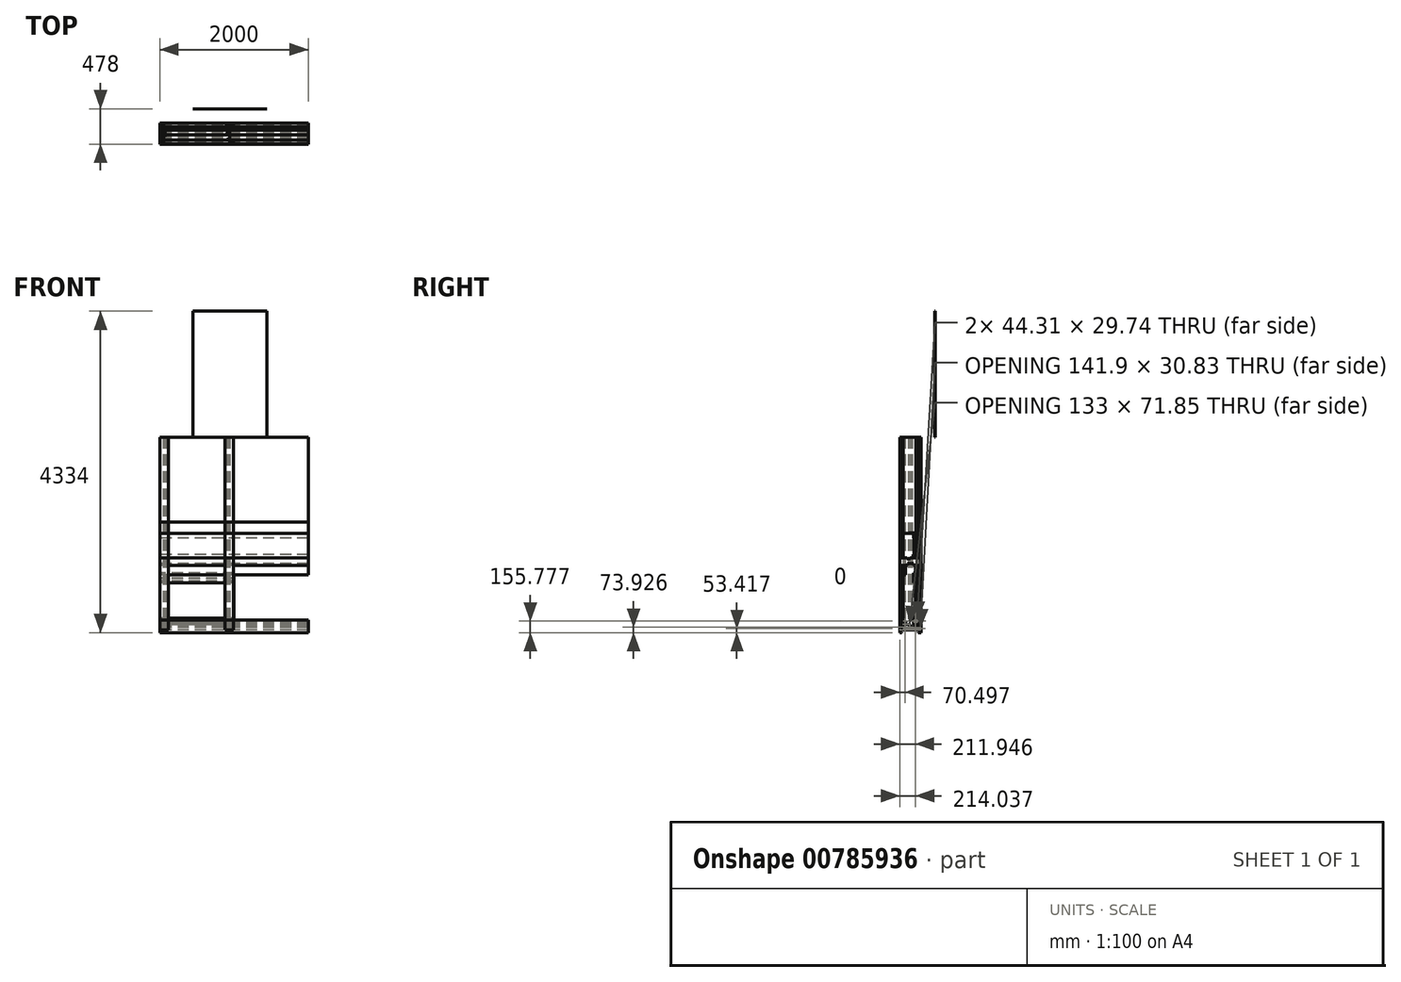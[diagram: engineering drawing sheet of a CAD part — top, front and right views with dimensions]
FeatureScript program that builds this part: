
annotation { "Feature Type Name" : "Feature", "Feature Type Description" : "" }
export const myFeature = defineFeature(function(context is Context, id is Id, definition is map)
    precondition{}
    {
        {
            var Q0;
            Q0=qCreatedBy(makeId("Top.planeOp"),FACE);
            var sketch = newSketch(context, id + "F0", { "sketchPlane" : qUnion([Q0])});
            skLineSegment(sketch, "E0", {"start": v(-131.77, 26.16) * mm, "end": v(-135.77, 26.16) * mm});
            skLineSegment(sketch, "E1", {"start": v(-135.77, 26.16) * mm, "end": v(-135.77, 70.16) * mm});
            skLineSegment(sketch, "E2", {"start": v(-135.77, 70.16) * mm, "end": v(-20.77, 70.16) * mm});
            skLineSegment(sketch, "E3", {"start": v(-20.77, 70.16) * mm, "end": v(-20.77, 66.16) * mm});
            skLineSegment(sketch, "E4", {"start": v(-20.77, 66.16) * mm, "end": v(-84.72, 66.16) * mm});
            skLineSegment(sketch, "E5", {"start": v(-84.72, 66.16) * mm, "end": v(-84.72, 4.73) * mm});
            skLineSegment(sketch, "E6", {"start": v(-84.72, 4.73) * mm, "end": v(-58.72, 4.73) * mm});
            skLineSegment(sketch, "E7", {"start": v(-58.72, 4.73) * mm, "end": v(-58.72, 6.73) * mm});
            skLineSegment(sketch, "E8", {"start": v(-58.72, 6.73) * mm, "end": v(-44.72, 0.73) * mm});
            skLineSegment(sketch, "E9", {"start": v(-44.72, 0.73) * mm, "end": v(-84.72, 0.73) * mm});
            skLineSegment(sketch, "E10", {"start": v(-84.72, 0.73) * mm, "end": v(-84.72, -93.45) * mm});
            skLineSegment(sketch, "E11", {"start": v(-84.72, -93.45) * mm, "end": v(-60.2, -93.45) * mm});
            skLineSegment(sketch, "E12", {"start": v(-60.2, -93.45) * mm, "end": v(-60.2, -73.83) * mm});
            skLineSegment(sketch, "E13", {"start": v(-60.2, -73.83) * mm, "end": v(-44.72, -73.83) * mm});
            skLineSegment(sketch, "E14", {"start": v(-44.72, -73.83) * mm, "end": v(-44.72, -79.83) * mm});
            skLineSegment(sketch, "E15", {"start": v(-44.72, -79.83) * mm, "end": v(-48.72, -79.83) * mm});
            skLineSegment(sketch, "E16", {"start": v(-48.72, -79.83) * mm, "end": v(-48.72, -77.83) * mm});
            skLineSegment(sketch, "E17", {"start": v(-48.72, -77.83) * mm, "end": v(-56.2, -77.83) * mm});
            skLineSegment(sketch, "E18", {"start": v(-56.2, -77.83) * mm, "end": v(-56.2, -93.45) * mm});
            skLineSegment(sketch, "E19", {"start": v(-56.2, -93.45) * mm, "end": v(-48.72, -93.45) * mm});
            skLineSegment(sketch, "E20", {"start": v(-48.72, -93.45) * mm, "end": v(-48.72, -91.45) * mm});
            skLineSegment(sketch, "E21", {"start": v(-48.72, -91.45) * mm, "end": v(-44.72, -91.45) * mm});
            skLineSegment(sketch, "E22", {"start": v(-44.72, -91.45) * mm, "end": v(-44.72, -97.45) * mm});
            skLineSegment(sketch, "E23", {"start": v(-44.72, -97.45) * mm, "end": v(-84.72, -97.45) * mm});
            skLineSegment(sketch, "E24", {"start": v(-84.72, -97.45) * mm, "end": v(-84.72, -212.73) * mm});
            skLineSegment(sketch, "E25", {"start": v(-84.72, -212.73) * mm, "end": v(-20.77, -212.73) * mm});
            skLineSegment(sketch, "E26", {"start": v(-20.77, -212.73) * mm, "end": v(-20.77, -216.73) * mm});
            skLineSegment(sketch, "E27", {"start": v(-20.77, -216.73) * mm, "end": v(-135.77, -216.73) * mm});
            skLineSegment(sketch, "E28", {"start": v(-135.77, -216.73) * mm, "end": v(-135.77, -172.73) * mm});
            skLineSegment(sketch, "E29", {"start": v(-135.77, -172.73) * mm, "end": v(-131.77, -172.73) * mm});
            skLineSegment(sketch, "E30", {"start": v(-131.77, -172.73) * mm, "end": v(-131.77, -212.73) * mm});
            skLineSegment(sketch, "E31", {"start": v(-131.77, -212.73) * mm, "end": v(-88.72, -212.73) * mm});
            skLineSegment(sketch, "E32", {"start": v(-88.72, -212.73) * mm, "end": v(-88.72, 66.16) * mm});
            skLineSegment(sketch, "E33", {"start": v(-88.72, 66.16) * mm, "end": v(-131.77, 66.16) * mm});
            skLineSegment(sketch, "E34", {"start": v(-131.77, 66.16) * mm, "end": v(-131.77, 26.16) * mm});
            skLineSegment(sketch, "E35.MirrorCS", {"start": v(763.76, -72.74) * mm, "end": v(763.76, -66.74) * mm});
            skLineSegment(sketch, "E36.MirrorCS", {"start": v(767.76, -66.74) * mm, "end": v(767.76, -68.74) * mm});
            skLineSegment(sketch, "E37.MirrorCS", {"start": v(767.76, -68.74) * mm, "end": v(775.23, -68.74) * mm});
            skLineSegment(sketch, "E38.MirrorCS", {"start": v(775.23, -68.74) * mm, "end": v(775.23, -53.12) * mm});
            skLineSegment(sketch, "E39.MirrorCS", {"start": v(779.23, -72.74) * mm, "end": v(763.76, -72.74) * mm});
            skLineSegment(sketch, "E40.MirrorCS", {"start": v(767.76, -53.12) * mm, "end": v(767.76, -55.12) * mm});
            skLineSegment(sketch, "E41.MirrorCS", {"start": v(763.76, -66.74) * mm, "end": v(767.76, -66.74) * mm});
            skLineSegment(sketch, "E42.MirrorCS", {"start": v(767.76, -55.12) * mm, "end": v(763.76, -55.12) * mm});
            skLineSegment(sketch, "E43.MirrorCS", {"start": v(763.76, -55.12) * mm, "end": v(763.76, -49.12) * mm});
            skLineSegment(sketch, "E44.MirrorCS", {"start": v(775.23, -53.12) * mm, "end": v(767.76, -53.12) * mm});
            skLineSegment(sketch, "E45.MirrorCS", {"start": v(779.23, -53.12) * mm, "end": v(779.23, -72.74) * mm});
            skLineSegment(sketch, "E46.MirrorCS", {"start": v(763.76, -49.12) * mm, "end": v(803.76, -49.12) * mm});
            skLineSegment(sketch, "E47.MirrorCS", {"start": v(803.76, -53.12) * mm, "end": v(779.23, -53.12) * mm});
            skLineSegment(sketch, "E48.MirrorCS", {"start": v(777.76, -153.3) * mm, "end": v(763.76, -147.3) * mm});
            skLineSegment(sketch, "E49.MirrorCS", {"start": v(850.81, -172.73) * mm, "end": v(854.81, -172.73) * mm});
            skLineSegment(sketch, "E50.MirrorCS", {"start": v(803.76, -151.3) * mm, "end": v(777.76, -151.3) * mm});
            skLineSegment(sketch, "E51.MirrorCS", {"start": v(777.76, -151.3) * mm, "end": v(777.76, -153.3) * mm});
            skLineSegment(sketch, "E52.MirrorCS", {"start": v(763.76, -147.3) * mm, "end": v(803.76, -147.3) * mm});
            skLineSegment(sketch, "E53.MirrorCS", {"start": v(739.81, -216.73) * mm, "end": v(739.81, -212.73) * mm});
            skLineSegment(sketch, "E54.MirrorCS", {"start": v(854.81, -0.01) * mm, "end": v(850.81, -0.01) * mm});
            skLineSegment(sketch, "E55.MirrorCS", {"start": v(739.81, 39.99) * mm, "end": v(739.81, 43.99) * mm});
            skLineSegment(sketch, "E56.MirrorCS", {"start": v(850.81, 39.99) * mm, "end": v(807.76, 39.99) * mm});
            skLineSegment(sketch, "E57.MirrorCS", {"start": v(803.76, -49.12) * mm, "end": v(803.76, 39.99) * mm});
            skLineSegment(sketch, "E58.MirrorCS", {"start": v(854.81, -172.73) * mm, "end": v(854.81, -216.73) * mm});
            skLineSegment(sketch, "E59.MirrorCS", {"start": v(807.76, -212.73) * mm, "end": v(850.81, -212.73) * mm});
            skLineSegment(sketch, "E60.MirrorCS", {"start": v(850.81, -0.01) * mm, "end": v(850.81, 39.99) * mm});
            skLineSegment(sketch, "E61.MirrorCS", {"start": v(854.81, -216.73) * mm, "end": v(739.81, -216.73) * mm});
            skLineSegment(sketch, "E62.MirrorCS", {"start": v(850.81, -212.73) * mm, "end": v(850.81, -172.73) * mm});
            skLineSegment(sketch, "E63.MirrorCS", {"start": v(803.76, 39.99) * mm, "end": v(739.81, 39.99) * mm});
            skLineSegment(sketch, "E64.MirrorCS", {"start": v(803.76, -147.3) * mm, "end": v(803.76, -53.12) * mm});
            skLineSegment(sketch, "E65.MirrorCS", {"start": v(803.76, -212.73) * mm, "end": v(803.76, -151.3) * mm});
            skLineSegment(sketch, "E66.MirrorCS", {"start": v(739.81, -212.73) * mm, "end": v(803.76, -212.73) * mm});
            skLineSegment(sketch, "E67.MirrorCS", {"start": v(854.81, 43.99) * mm, "end": v(854.81, -0.01) * mm});
            skLineSegment(sketch, "E68.MirrorCS", {"start": v(807.76, 39.99) * mm, "end": v(807.76, -212.73) * mm});
            skLineSegment(sketch, "E69.MirrorCS", {"start": v(739.81, 43.99) * mm, "end": v(854.81, 43.99) * mm});
            skSolve(sketch);
        }
        {
            var Q0;
            Q0=makeQuery(id+"F0.imprint","IMPRINT",FACE,{"disambiguationData":[TD([[makeQuery(id+"F0.imprint","IMPRINT",EDGE,{"derivedFrom":sQuery(id+"F0.wireOp",EDGE,"E0")}),-1.0]])]});
            extrude(context, id + "F1", {"entities" : qUnion([Q0]), "depth" : 2600 * mm, "offsetDistance" : 25 * mm});
        }
        {
            var Q0;
            Q0=makeQuery(id+"F0.imprint","IMPRINT",FACE,{"disambiguationData":[TD([[makeQuery(id+"F0.imprint","IMPRINT",EDGE,{"derivedFrom":sQuery(id+"F0.wireOp",EDGE,"E35.MirrorCS")}),-1.0]])]});
            extrude(context, id + "F2", {"entities" : qUnion([Q0]), "depth" : 2600 * mm, "offsetDistance" : 25 * mm});
        }
        {
            var Q0;
            Q0=makeQuery(id+"F1.opExtrude","SWEPT_FACE",FACE,{"disambiguationData":[OSD([sQuery(id+"F0.wireOp",EDGE,"E28")])]});
            var sketch = newSketch(context, id + "F3", { "sketchPlane" : qUnion([Q0])});
            skLineSegment(sketch, "E70", {"start": v(-70.16, -34) * mm, "end": v(-70.16, 69.03) * mm});
            skLineSegment(sketch, "E71", {"start": v(-70.16, 69.03) * mm, "end": v(-66.16, 69.03) * mm});
            skLineSegment(sketch, "E72", {"start": v(-66.16, 69.03) * mm, "end": v(-66.16, 36.25) * mm});
            skLineSegment(sketch, "E73", {"start": v(-66.16, 36.25) * mm, "end": v(-11.46, 36.25) * mm});
            skLineSegment(sketch, "E74", {"start": v(0, 38.83) * mm, "end": v(0, 88.3) * mm});
            skLineSegment(sketch, "E75", {"start": v(0, 88.3) * mm, "end": v(-6.87, 88.3) * mm});
            skLineSegment(sketch, "E76", {"start": v(-6.87, 88.3) * mm, "end": v(-6.87, 76.3) * mm});
            skLineSegment(sketch, "E77", {"start": v(-6.87, 76.3) * mm, "end": v(-11.46, 76.3) * mm});
            skLineSegment(sketch, "E78", {"start": v(-11.46, 76.3) * mm, "end": v(-11.46, 92.3) * mm});
            skLineSegment(sketch, "E79", {"start": v(-11.46, 92.3) * mm, "end": v(16.85, 92.3) * mm});
            skLineSegment(sketch, "E80", {"start": v(16.85, 92.3) * mm, "end": v(16.85, 76.3) * mm});
            skLineSegment(sketch, "E81", {"start": v(16.85, 76.3) * mm, "end": v(12.85, 76.3) * mm});
            skLineSegment(sketch, "E82", {"start": v(12.85, 76.3) * mm, "end": v(12.85, 88.3) * mm});
            skLineSegment(sketch, "E83", {"start": v(12.85, 88.3) * mm, "end": v(4, 88.3) * mm});
            skLineSegment(sketch, "E84", {"start": v(4, 88.3) * mm, "end": v(4, 38.83) * mm});
            skLineSegment(sketch, "E85", {"start": v(-70.16, -34) * mm, "end": v(-32.13, -34) * mm});
            skLineSegment(sketch, "E86", {"start": v(-32.13, -34) * mm, "end": v(-32.13, -30) * mm});
            skLineSegment(sketch, "E87", {"start": v(-32.13, -30) * mm, "end": v(-66.16, -30) * mm});
            skLineSegment(sketch, "E88", {"start": v(-66.16, -30) * mm, "end": v(-66.16, 0) * mm});
            skLineSegment(sketch, "E89", {"start": v(-66.16, 0) * mm, "end": v(212.73, 0) * mm});
            skLineSegment(sketch, "E90", {"start": v(212.73, -30) * mm, "end": v(187.57, -30) * mm});
            skLineSegment(sketch, "E91", {"start": v(187.57, -30) * mm, "end": v(187.57, -34) * mm});
            skLineSegment(sketch, "E92", {"start": v(187.57, -34) * mm, "end": v(216.73, -34) * mm});
            skLineSegment(sketch, "E93", {"start": v(216.73, -34) * mm, "end": v(216.73, 138.64) * mm});
            skLineSegment(sketch, "E94", {"start": v(216.73, 138.64) * mm, "end": v(212.73, 138.64) * mm});
            skLineSegment(sketch, "E95", {"start": v(212.73, 138.64) * mm, "end": v(212.73, 113.43) * mm});
            skLineSegment(sketch, "E96", {"start": v(212.73, 113.43) * mm, "end": v(206.73, 113.43) * mm});
            skLineSegment(sketch, "E97", {"start": v(206.73, 113.43) * mm, "end": v(206.73, 107.43) * mm});
            skLineSegment(sketch, "E98", {"start": v(206.73, 107.43) * mm, "end": v(210.73, 107.43) * mm});
            skLineSegment(sketch, "E99", {"start": v(210.73, 107.43) * mm, "end": v(210.73, 109.43) * mm});
            skLineSegment(sketch, "E100", {"start": v(210.73, 109.43) * mm, "end": v(212.73, 109.43) * mm});
            skLineSegment(sketch, "E101", {"start": v(212.73, 109.43) * mm, "end": v(212.73, 88) * mm});
            skLineSegment(sketch, "E102", {"start": v(212.73, 88) * mm, "end": v(210.73, 88) * mm});
            skLineSegment(sketch, "E103", {"start": v(210.73, 88) * mm, "end": v(210.73, 90) * mm});
            skLineSegment(sketch, "E104", {"start": v(210.73, 90) * mm, "end": v(206.73, 90) * mm});
            skLineSegment(sketch, "E105", {"start": v(206.73, 90) * mm, "end": v(206.73, 84) * mm});
            skLineSegment(sketch, "E106", {"start": v(206.73, 84) * mm, "end": v(212.73, 84) * mm});
            skLineSegment(sketch, "E107", {"start": v(212.73, 84) * mm, "end": v(212.73, 79.86) * mm});
            skLineSegment(sketch, "E108", {"start": v(212.73, -30) * mm, "end": v(212.73, 0) * mm});
            skLineSegment(sketch, "E109", {"start": v(212.73, 4) * mm, "end": v(79.73, 4) * mm});
            skLineSegment(sketch, "E110", {"start": v(72.84, 551.08) * mm, "end": v(72.84, 267.71) * mm, "construction": true});
            skLineSegment(sketch, "E111", {"start": v(146.73, 79.86) * mm, "end": v(146.73, 115.55) * mm});
            skLineSegment(sketch, "E112", {"start": v(150.73, 115.55) * mm, "end": v(150.73, 103.55) * mm});
            skLineSegment(sketch, "E113", {"start": v(150.73, 103.55) * mm, "end": v(154.73, 103.55) * mm});
            skLineSegment(sketch, "E114", {"start": v(154.73, 103.55) * mm, "end": v(154.73, 119.55) * mm});
            skLineSegment(sketch, "E115", {"start": v(154.73, 119.55) * mm, "end": v(134.73, 119.55) * mm});
            skLineSegment(sketch, "E116", {"start": v(134.73, 119.55) * mm, "end": v(134.73, 103.55) * mm});
            skLineSegment(sketch, "E117", {"start": v(134.73, 103.55) * mm, "end": v(138.73, 103.55) * mm});
            skLineSegment(sketch, "E118", {"start": v(138.73, 103.55) * mm, "end": v(138.73, 115.55) * mm});
            skLineSegment(sketch, "E119", {"start": v(138.73, 115.55) * mm, "end": v(142.73, 115.55) * mm});
            skLineSegment(sketch, "E120", {"start": v(142.73, 115.55) * mm, "end": v(142.73, 79.86) * mm});
            skLineSegment(sketch, "E121", {"start": v(142.73, 79.86) * mm, "end": v(67.73, 74.54) * mm});
            skLineSegment(sketch, "E122", {"start": v(67.73, 74.54) * mm, "end": v(67.73, 62.44) * mm});
            skLineSegment(sketch, "E123", {"start": v(67.73, 62.44) * mm, "end": v(71.73, 62.44) * mm});
            skLineSegment(sketch, "E124", {"start": v(71.73, 62.44) * mm, "end": v(71.73, 66.44) * mm});
            skLineSegment(sketch, "E125", {"start": v(71.73, 66.44) * mm, "end": v(75.73, 66.44) * mm});
            skLineSegment(sketch, "E126", {"start": v(75.73, 66.44) * mm, "end": v(75.73, 50.83) * mm});
            skLineSegment(sketch, "E127", {"start": v(75.73, 50.83) * mm, "end": v(71.73, 50.83) * mm});
            skLineSegment(sketch, "E128", {"start": v(71.73, 50.83) * mm, "end": v(71.73, 54.83) * mm});
            skLineSegment(sketch, "E129", {"start": v(71.73, 54.83) * mm, "end": v(67.73, 54.83) * mm});
            skLineSegment(sketch, "E130", {"start": v(67.73, 54.83) * mm, "end": v(67.73, 46.83) * mm});
            skLineSegment(sketch, "E131", {"start": v(67.73, 46.83) * mm, "end": v(75.73, 46.83) * mm});
            skLineSegment(sketch, "E132", {"start": v(75.73, 46.83) * mm, "end": v(75.73, 38.83) * mm});
            skLineSegment(sketch, "E133", {"start": v(75.73, 38.83) * mm, "end": v(4, 38.83) * mm});
            skLineSegment(sketch, "E134", {"start": v(146.73, 115.55) * mm, "end": v(150.73, 115.55) * mm});
            skLineSegment(sketch, "E135", {"start": v(146.73, 79.86) * mm, "end": v(212.73, 79.86) * mm});
            skLineSegment(sketch, "E136", {"start": v(212.73, 75.85) * mm, "end": v(142.73, 75.85) * mm});
            skLineSegment(sketch, "E137.trimOffspring", {"start": v(212.73, 75.85) * mm, "end": v(212.73, 4) * mm});
            skLineSegment(sketch, "E138", {"start": v(79.73, 71.38) * mm, "end": v(79.73, 4) * mm});
            skLineSegment(sketch, "E139", {"start": v(142.73, 75.85) * mm, "end": v(79.73, 71.38) * mm});
            skLineSegment(sketch, "E140", {"start": v(75.73, 4) * mm, "end": v(75.73, 34.83) * mm});
            skLineSegment(sketch, "E141", {"start": v(75.73, 34.83) * mm, "end": v(-0.59, 34.83) * mm});
            skLineSegment(sketch, "E142", {"start": v(-12.05, 32.25) * mm, "end": v(-66.16, 32.25) * mm});
            skLineSegment(sketch, "E143", {"start": v(-66.16, 32.25) * mm, "end": v(-66.16, 4) * mm});
            skLineSegment(sketch, "E144", {"start": v(-66.16, 4) * mm, "end": v(75.73, 4) * mm});
            skLineSegment(sketch, "E145", {"start": v(-11.46, 36.25) * mm, "end": v(0, 38.83) * mm});
            skLineSegment(sketch, "E146", {"start": v(-12.05, 32.25) * mm, "end": v(-0.59, 34.83) * mm});
            skSolve(sketch);
        }
        {
            var Q0;
            Q0 = qSketchRegion(id + "F3", true);
            extrude(context, id + "F4", {"entities" : qUnion([Q0]), "oppositeDirection" : true, "depth" : 2000 * mm, "offsetDistance" : 25 * mm});
        }
        {
            var Q0;
            Q0=makeQuery(id+"F1.opExtrude","SWEPT_FACE",FACE,{"disambiguationData":[OSD([sQuery(id+"F0.wireOp",EDGE,"E1")])]});
            var sketch = newSketch(context, id + "F5", { "sketchPlane" : qUnion([Q0])});
            skLineSegment(sketch, "E147", {"start": v(-70.16, 972.5) * mm, "end": v(-70.16, 2600) * mm});
            skLineSegment(sketch, "E148", {"start": v(-70.16, 972.5) * mm, "end": v(-14.46, 972.5) * mm});
            skLineSegment(sketch, "E149", {"start": v(-14.46, 972.5) * mm, "end": v(-14.46, 1017.43) * mm});
            skLineSegment(sketch, "E150", {"start": v(-14.46, 1017.43) * mm, "end": v(-10.46, 1017.43) * mm});
            skLineSegment(sketch, "E151", {"start": v(-10.46, 1017.43) * mm, "end": v(-10.46, 972.5) * mm});
            skLineSegment(sketch, "E152", {"start": v(-10.46, 972.5) * mm, "end": v(30.91, 972.5) * mm});
            skLineSegment(sketch, "E153", {"start": v(72.28, 972.5) * mm, "end": v(72.28, 964.5) * mm});
            skLineSegment(sketch, "E154", {"start": v(72.28, 964.5) * mm, "end": v(116.6, 964.5) * mm});
            skLineSegment(sketch, "E155", {"start": v(116.6, 964.5) * mm, "end": v(116.6, 972.5) * mm});
            skLineSegment(sketch, "E156", {"start": v(116.6, 972.5) * mm, "end": v(216.73, 972.5) * mm});
            skLineSegment(sketch, "E157", {"start": v(216.73, 2600) * mm, "end": v(216.73, 972.5) * mm});
            skLineSegment(sketch, "E158", {"start": v(-70.16, 2600) * mm, "end": v(-66.16, 2600) * mm});
            skLineSegment(sketch, "E159", {"start": v(-66.16, 875.29) * mm, "end": v(-66.16, 2600) * mm});
            skLineSegment(sketch, "E160", {"start": v(-66.16, 875.29) * mm, "end": v(1.84, 875.29) * mm});
            skLineSegment(sketch, "E161", {"start": v(1.84, 875.29) * mm, "end": v(1.84, 748.56) * mm});
            skLineSegment(sketch, "E162", {"start": v(1.84, 748.56) * mm, "end": v(5.84, 748.56) * mm});
            skLineSegment(sketch, "E163", {"start": v(5.84, 748.56) * mm, "end": v(5.84, 875.29) * mm});
            skLineSegment(sketch, "E164", {"start": v(5.84, 875.29) * mm, "end": v(33.47, 875.29) * mm});
            skLineSegment(sketch, "E165", {"start": v(33.47, 875.29) * mm, "end": v(33.47, 898.4) * mm});
            skLineSegment(sketch, "E166", {"start": v(33.47, 898.4) * mm, "end": v(112.2, 898.4) * mm});
            skLineSegment(sketch, "E167", {"start": v(30.91, 972.5) * mm, "end": v(30.91, 1017.1) * mm});
            skLineSegment(sketch, "E168", {"start": v(30.91, 1017.1) * mm, "end": v(34.91, 1017.1) * mm});
            skLineSegment(sketch, "E169", {"start": v(34.91, 1017.1) * mm, "end": v(34.91, 972.5) * mm});
            skLineSegment(sketch, "E170.trimOffspring", {"start": v(34.91, 972.5) * mm, "end": v(72.28, 972.5) * mm});
            skLineSegment(sketch, "E171", {"start": v(-66.16, 879.29) * mm, "end": v(-66.16, 968.5) * mm});
            skLineSegment(sketch, "E172", {"start": v(-66.16, 968.5) * mm, "end": v(68.28, 968.5) * mm});
            skLineSegment(sketch, "E173", {"start": v(68.28, 968.5) * mm, "end": v(68.28, 960.5) * mm});
            skLineSegment(sketch, "E174", {"start": v(68.28, 960.5) * mm, "end": v(120.6, 960.5) * mm});
            skLineSegment(sketch, "E175", {"start": v(120.6, 960.5) * mm, "end": v(120.6, 966.67) * mm});
            skLineSegment(sketch, "E176", {"start": v(120.6, 966.67) * mm, "end": v(212.73, 966.67) * mm});
            skLineSegment(sketch, "E177", {"start": v(212.73, 966.67) * mm, "end": v(212.73, 879.29) * mm});
            skLineSegment(sketch, "E178", {"start": v(-66.16, 879.29) * mm, "end": v(29.47, 879.29) * mm});
            skLineSegment(sketch, "E179", {"start": v(29.47, 879.29) * mm, "end": v(29.47, 902.4) * mm});
            skLineSegment(sketch, "E180", {"start": v(29.47, 902.4) * mm, "end": v(116.2, 902.4) * mm});
            skLineSegment(sketch, "E181.MirrorCS", {"start": v(112.2, 875.29) * mm, "end": v(112.2, 898.4) * mm});
            skLineSegment(sketch, "E182.MirrorCS", {"start": v(116.2, 879.29) * mm, "end": v(116.2, 902.4) * mm});
            skLineSegment(sketch, "E183.MirrorCS", {"start": v(211.84, 879.29) * mm, "end": v(116.2, 879.29) * mm});
            skLineSegment(sketch, "E184.MirrorCS", {"start": v(211.84, 875.29) * mm, "end": v(143.84, 875.29) * mm});
            skLineSegment(sketch, "E185.MirrorCS", {"start": v(143.84, 748.56) * mm, "end": v(139.84, 748.56) * mm});
            skLineSegment(sketch, "E186.MirrorCS", {"start": v(139.84, 748.56) * mm, "end": v(139.84, 875.29) * mm});
            skLineSegment(sketch, "E187.MirrorCS", {"start": v(143.84, 875.29) * mm, "end": v(143.84, 748.56) * mm});
            skLineSegment(sketch, "E188.MirrorCS", {"start": v(139.84, 875.29) * mm, "end": v(112.2, 875.29) * mm});
            skLineSegment(sketch, "E189", {"start": v(216.73, 2600) * mm, "end": v(212.73, 2600) * mm});
            skLineSegment(sketch, "E190", {"start": v(212.73, 875.29) * mm, "end": v(212.73, 2600) * mm});
            skLineSegment(sketch, "E191", {"start": v(211.84, 879.29) * mm, "end": v(212.73, 879.29) * mm});
            skLineSegment(sketch, "E192", {"start": v(211.84, 875.29) * mm, "end": v(212.73, 875.29) * mm});
            skSolve(sketch);
        }
        {
            var Q0;
            Q0 = qSketchRegion(id + "F5", true);
            extrude(context, id + "F6", {"entities" : qUnion([Q0]), "oppositeDirection" : true, "depth" : 2000 * mm, "offsetDistance" : 25 * mm});
        }
        {
            var Q0;
            Q0=makeQuery(id+"F6.opExtrude","CAP_FACE",FACE,{"disambiguationData":[OSD([sQuery(id+"F5.wireOp",EDGE,"E147"),sQuery(id+"F5.wireOp",EDGE,"E148"),sQuery(id+"F5.wireOp",EDGE,"E149"),sQuery(id+"F5.wireOp",EDGE,"E150"),sQuery(id+"F5.wireOp",EDGE,"E151"),sQuery(id+"F5.wireOp",EDGE,"E152"),sQuery(id+"F5.wireOp",EDGE,"E153"),sQuery(id+"F5.wireOp",EDGE,"E154"),sQuery(id+"F5.wireOp",EDGE,"E155"),sQuery(id+"F5.wireOp",EDGE,"E156"),sQuery(id+"F5.wireOp",EDGE,"E157"),sQuery(id+"F5.wireOp",EDGE,"E158"),sQuery(id+"F5.wireOp",EDGE,"E159"),sQuery(id+"F5.wireOp",EDGE,"E160"),sQuery(id+"F5.wireOp",EDGE,"E161"),sQuery(id+"F5.wireOp",EDGE,"E162"),sQuery(id+"F5.wireOp",EDGE,"E163"),sQuery(id+"F5.wireOp",EDGE,"E164"),sQuery(id+"F5.wireOp",EDGE,"E165"),sQuery(id+"F5.wireOp",EDGE,"E166"),sQuery(id+"F5.wireOp",EDGE,"E167"),sQuery(id+"F5.wireOp",EDGE,"E168"),sQuery(id+"F5.wireOp",EDGE,"E169"),sQuery(id+"F5.wireOp",EDGE,"E170.trimOffspring"),sQuery(id+"F5.wireOp",EDGE,"E171"),sQuery(id+"F5.wireOp",EDGE,"E172"),sQuery(id+"F5.wireOp",EDGE,"E173"),sQuery(id+"F5.wireOp",EDGE,"E174"),sQuery(id+"F5.wireOp",EDGE,"E175"),sQuery(id+"F5.wireOp",EDGE,"E176"),sQuery(id+"F5.wireOp",EDGE,"E177"),sQuery(id+"F5.wireOp",EDGE,"E178"),sQuery(id+"F5.wireOp",EDGE,"E179"),sQuery(id+"F5.wireOp",EDGE,"E180"),sQuery(id+"F5.wireOp",EDGE,"E181.MirrorCS"),sQuery(id+"F5.wireOp",EDGE,"E182.MirrorCS"),sQuery(id+"F5.wireOp",EDGE,"E183.MirrorCS"),sQuery(id+"F5.wireOp",EDGE,"E184.MirrorCS"),sQuery(id+"F5.wireOp",EDGE,"E185.MirrorCS"),sQuery(id+"F5.wireOp",EDGE,"E186.MirrorCS"),sQuery(id+"F5.wireOp",EDGE,"E187.MirrorCS"),sQuery(id+"F5.wireOp",EDGE,"E188.MirrorCS"),sQuery(id+"F5.wireOp",EDGE,"E189"),sQuery(id+"F5.wireOp",EDGE,"E190"),sQuery(id+"F5.wireOp",EDGE,"E191"),sQuery(id+"F5.wireOp",EDGE,"E192")])],"isStart":true});
            var sketch = newSketch(context, id + "F7", { "sketchPlane" : qUnion([Q0])});
            skLineSegment(sketch, "E193", {"start": v(-10.46, 1243.09) * mm, "end": v(-10.46, 1302.74) * mm});
            skLineSegment(sketch, "E194", {"start": v(-10.46, 1302.74) * mm, "end": v(26.58, 1302.74) * mm});
            skLineSegment(sketch, "E195", {"start": v(30.91, 1302.74) * mm, "end": v(30.91, 1306.74) * mm});
            skLineSegment(sketch, "E196", {"start": v(30.91, 1306.74) * mm, "end": v(87.31, 1306.74) * mm});
            skLineSegment(sketch, "E197", {"start": v(87.31, 1306.74) * mm, "end": v(87.31, 1302.74) * mm});
            skLineSegment(sketch, "E198", {"start": v(87.31, 1302.74) * mm, "end": v(216.73, 1302.74) * mm});
            skLineSegment(sketch, "E199", {"start": v(216.73, 1302.74) * mm, "end": v(216.73, 1459.6) * mm});
            skLineSegment(sketch, "E200", {"start": v(216.73, 1459.6) * mm, "end": v(160.6, 1459.6) * mm});
            skLineSegment(sketch, "E201", {"start": v(160.6, 1459.6) * mm, "end": v(160.6, 1455.6) * mm});
            skLineSegment(sketch, "E202", {"start": v(160.6, 1455.6) * mm, "end": v(212.73, 1455.6) * mm});
            skLineSegment(sketch, "E203", {"start": v(212.73, 1455.6) * mm, "end": v(212.73, 1306.74) * mm});
            skLineSegment(sketch, "E204", {"start": v(212.73, 1306.74) * mm, "end": v(91.31, 1306.74) * mm});
            skLineSegment(sketch, "E205", {"start": v(91.31, 1306.74) * mm, "end": v(91.31, 1310.74) * mm});
            skLineSegment(sketch, "E206", {"start": v(91.31, 1310.74) * mm, "end": v(26.91, 1310.74) * mm});
            skLineSegment(sketch, "E207", {"start": v(26.91, 1310.74) * mm, "end": v(26.91, 1306.74) * mm});
            skLineSegment(sketch, "E208", {"start": v(30.91, 1243.09) * mm, "end": v(30.91, 1302.74) * mm});
            skLineSegment(sketch, "E209", {"start": v(-10.46, 1243.09) * mm, "end": v(-14.46, 1243.09) * mm});
            skLineSegment(sketch, "E210", {"start": v(-14.46, 1243.09) * mm, "end": v(-14.46, 1302.74) * mm});
            skLineSegment(sketch, "E211", {"start": v(-14.46, 1302.74) * mm, "end": v(-70.16, 1302.74) * mm});
            skLineSegment(sketch, "E212", {"start": v(-70.16, 1302.74) * mm, "end": v(-70.16, 1458.04) * mm});
            skLineSegment(sketch, "E213", {"start": v(-70.16, 1458.04) * mm, "end": v(-14.46, 1458.04) * mm});
            skLineSegment(sketch, "E214", {"start": v(-14.46, 1458.04) * mm, "end": v(-14.46, 1454.04) * mm});
            skLineSegment(sketch, "E215", {"start": v(-14.46, 1454.04) * mm, "end": v(-66.16, 1454.04) * mm});
            skLineSegment(sketch, "E216", {"start": v(-66.16, 1454.04) * mm, "end": v(-66.16, 1306.74) * mm});
            skLineSegment(sketch, "E217", {"start": v(-66.16, 1306.74) * mm, "end": v(0, 1306.74) * mm});
            skLineSegment(sketch, "E218", {"start": v(0, 1306.74) * mm, "end": v(26.91, 1306.74) * mm});
            skLineSegment(sketch, "E219", {"start": v(30.91, 1243.09) * mm, "end": v(26.58, 1243.09) * mm});
            skLineSegment(sketch, "E220", {"start": v(26.58, 1243.09) * mm, "end": v(26.58, 1302.74) * mm});
            skSolve(sketch);
        }
        {
            var Q0;
            Q0 = qSketchRegion(id + "F7", true);
            extrude(context, id + "F8", {"entities" : qUnion([Q0]), "oppositeDirection" : true, "depth" : 2000 * mm, "offsetDistance" : 25 * mm});
        }
        {
            var Q0;
            Q0=makeQuery(id+"F8.opExtrude","CAP_FACE",FACE,{"disambiguationData":[OSD([sQuery(id+"F7.wireOp",EDGE,"E193"),sQuery(id+"F7.wireOp",EDGE,"E194"),sQuery(id+"F7.wireOp",EDGE,"E195"),sQuery(id+"F7.wireOp",EDGE,"E196"),sQuery(id+"F7.wireOp",EDGE,"E197"),sQuery(id+"F7.wireOp",EDGE,"E198"),sQuery(id+"F7.wireOp",EDGE,"E199"),sQuery(id+"F7.wireOp",EDGE,"E200"),sQuery(id+"F7.wireOp",EDGE,"E201"),sQuery(id+"F7.wireOp",EDGE,"E202"),sQuery(id+"F7.wireOp",EDGE,"E203"),sQuery(id+"F7.wireOp",EDGE,"E204"),sQuery(id+"F7.wireOp",EDGE,"E205"),sQuery(id+"F7.wireOp",EDGE,"E206"),sQuery(id+"F7.wireOp",EDGE,"E207"),sQuery(id+"F7.wireOp",EDGE,"E208"),sQuery(id+"F7.wireOp",EDGE,"E209"),sQuery(id+"F7.wireOp",EDGE,"E210"),sQuery(id+"F7.wireOp",EDGE,"E211"),sQuery(id+"F7.wireOp",EDGE,"E212"),sQuery(id+"F7.wireOp",EDGE,"E213"),sQuery(id+"F7.wireOp",EDGE,"E214"),sQuery(id+"F7.wireOp",EDGE,"E215"),sQuery(id+"F7.wireOp",EDGE,"E216"),sQuery(id+"F7.wireOp",EDGE,"E217"),sQuery(id+"F7.wireOp",EDGE,"E218"),sQuery(id+"F7.wireOp",EDGE,"E219"),sQuery(id+"F7.wireOp",EDGE,"E220")])],"isStart":true});
            var sketch = newSketch(context, id + "F9", { "sketchPlane" : qUnion([Q0])});
            skLineSegment(sketch, "E221.bottom", {"start": v(-7.73, 1292.73) * mm, "end": v(24.3, 1292.73) * mm});
            skLineSegment(sketch, "E221.top", {"start": v(-7.73, 977.48) * mm, "end": v(24.3, 977.48) * mm});
            skLineSegment(sketch, "E221.left", {"start": v(-7.73, 1292.73) * mm, "end": v(-7.73, 977.48) * mm});
            skLineSegment(sketch, "E221.right", {"start": v(24.3, 1292.73) * mm, "end": v(24.3, 977.48) * mm});
            skSolve(sketch);
        }
        {
            var Q0;
            Q0=makeQuery(id+"F9.imprint","IMPRINT",FACE,{"disambiguationData":[TD([[makeQuery(id+"F9.imprint","IMPRINT",EDGE,{"derivedFrom":sQuery(id+"F9.wireOp",EDGE,"E221.bottom")}),-1.0]])]});
            extrude(context, id + "F10", {"entities" : qUnion([Q0]), "oppositeDirection" : true, "depth" : 2000 * mm, "offsetDistance" : 25 * mm});
        }
        {
            var Q0;
            Q0=makeQuery(id+"F6.opExtrude","CAP_FACE",FACE,{"disambiguationData":[OSD([sQuery(id+"F5.wireOp",EDGE,"E148"),sQuery(id+"F5.wireOp",EDGE,"E149"),sQuery(id+"F5.wireOp",EDGE,"E150"),sQuery(id+"F5.wireOp",EDGE,"E151"),sQuery(id+"F5.wireOp",EDGE,"E152"),sQuery(id+"F5.wireOp",EDGE,"E153"),sQuery(id+"F5.wireOp",EDGE,"E154"),sQuery(id+"F5.wireOp",EDGE,"E155"),sQuery(id+"F5.wireOp",EDGE,"E156"),sQuery(id+"F5.wireOp",EDGE,"E159"),sQuery(id+"F5.wireOp",EDGE,"E160"),sQuery(id+"F5.wireOp",EDGE,"E161"),sQuery(id+"F5.wireOp",EDGE,"E162"),sQuery(id+"F5.wireOp",EDGE,"E163"),sQuery(id+"F5.wireOp",EDGE,"E164"),sQuery(id+"F5.wireOp",EDGE,"E165"),sQuery(id+"F5.wireOp",EDGE,"E166"),sQuery(id+"F5.wireOp",EDGE,"E167"),sQuery(id+"F5.wireOp",EDGE,"E168"),sQuery(id+"F5.wireOp",EDGE,"E169"),sQuery(id+"F5.wireOp",EDGE,"E170.trimOffspring"),sQuery(id+"F5.wireOp",EDGE,"E171"),sQuery(id+"F5.wireOp",EDGE,"E181.MirrorCS"),sQuery(id+"F5.wireOp",EDGE,"E184.MirrorCS"),sQuery(id+"F5.wireOp",EDGE,"E185.MirrorCS"),sQuery(id+"F5.wireOp",EDGE,"E186.MirrorCS"),sQuery(id+"F5.wireOp",EDGE,"E187.MirrorCS"),sQuery(id+"F5.wireOp",EDGE,"E188.MirrorCS"),sQuery(id+"F5.wireOp",EDGE,"E190"),sQuery(id+"F5.wireOp",EDGE,"E192")])],"isStart":true});
            var sketch = newSketch(context, id + "F11", { "sketchPlane" : qUnion([Q0])});
            skLineSegment(sketch, "E222", {"start": v(-8.81, 768.15) * mm, "end": v(-20.84, 768.15) * mm});
            skLineSegment(sketch, "E223", {"start": v(-20.84, 768.15) * mm, "end": v(-20.84, 638.71) * mm});
            skLineSegment(sketch, "E224", {"start": v(-20.84, 638.71) * mm, "end": v(-3.18, 638.71) * mm});
            skLineSegment(sketch, "E225", {"start": v(-3.18, 638.71) * mm, "end": v(-3.18, 661.2) * mm});
            skLineSegment(sketch, "E226", {"start": v(-3.18, 661.2) * mm, "end": v(-7.18, 661.2) * mm});
            skLineSegment(sketch, "E227", {"start": v(-7.18, 661.2) * mm, "end": v(-7.18, 643.15) * mm});
            skLineSegment(sketch, "E228", {"start": v(-7.18, 643.15) * mm, "end": v(-16.84, 643.15) * mm});
            skLineSegment(sketch, "E229", {"start": v(-16.84, 643.15) * mm, "end": v(-16.84, 694.48) * mm});
            skLineSegment(sketch, "E230", {"start": v(28.61, 638.71) * mm, "end": v(7.9, 638.94) * mm});
            skLineSegment(sketch, "E231", {"start": v(11.9, 643.93) * mm, "end": v(24.61, 643.87) * mm});
            skLineSegment(sketch, "E232", {"start": v(24.61, 643.87) * mm, "end": v(24.61, 694.48) * mm});
            skLineSegment(sketch, "E233", {"start": v(-16.84, 747.73) * mm, "end": v(-8.81, 747.73) * mm});
            skLineSegment(sketch, "E234", {"start": v(-8.81, 762.18) * mm, "end": v(-12.81, 762.18) * mm});
            skLineSegment(sketch, "E235", {"start": v(-12.81, 751.73) * mm, "end": v(-16.84, 751.73) * mm});
            skLineSegment(sketch, "E236", {"start": v(-16.84, 764.15) * mm, "end": v(-12.81, 764.15) * mm});
            skLineSegment(sketch, "E237", {"start": v(-12.81, 754.18) * mm, "end": v(-8.81, 754.18) * mm});
            skLineSegment(sketch, "E238", {"start": v(-16.84, 698.48) * mm, "end": v(24.61, 698.48) * mm});
            skLineSegment(sketch, "E239", {"start": v(24.61, 694.48) * mm, "end": v(-16.84, 694.48) * mm});
            skLineSegment(sketch, "E240.trimOffspring", {"start": v(-16.84, 698.48) * mm, "end": v(-16.84, 747.73) * mm});
            skLineSegment(sketch, "E241", {"start": v(24.61, 698.48) * mm, "end": v(24.61, 747.72) * mm});
            skLineSegment(sketch, "E242", {"start": v(24.61, 747.72) * mm, "end": v(16.61, 747.72) * mm});
            skLineSegment(sketch, "E243", {"start": v(16.61, 747.72) * mm, "end": v(16.61, 752.15) * mm});
            skLineSegment(sketch, "E244", {"start": v(16.61, 752.15) * mm, "end": v(20.61, 752.15) * mm});
            skLineSegment(sketch, "E245", {"start": v(24.61, 752.15) * mm, "end": v(24.61, 760.15) * mm});
            skLineSegment(sketch, "E246", {"start": v(20.61, 760.15) * mm, "end": v(16.61, 760.15) * mm});
            skLineSegment(sketch, "E247", {"start": v(16.61, 760.15) * mm, "end": v(16.61, 768.15) * mm});
            skLineSegment(sketch, "E248", {"start": v(16.61, 768.15) * mm, "end": v(28.61, 768.15) * mm});
            skLineSegment(sketch, "E249", {"start": v(20.61, 760.15) * mm, "end": v(20.61, 764.15) * mm});
            skLineSegment(sketch, "E250", {"start": v(20.61, 764.15) * mm, "end": v(24.61, 764.15) * mm});
            skLineSegment(sketch, "E251", {"start": v(24.61, 764.15) * mm, "end": v(24.61, 760.15) * mm});
            skLineSegment(sketch, "E252", {"start": v(24.61, 752.15) * mm, "end": v(24.61, 750.2) * mm});
            skLineSegment(sketch, "E253", {"start": v(24.61, 750.2) * mm, "end": v(20.61, 750.2) * mm});
            skLineSegment(sketch, "E254", {"start": v(20.61, 750.2) * mm, "end": v(20.61, 752.15) * mm});
            skLineSegment(sketch, "E255", {"start": v(-8.81, 768.15) * mm, "end": v(-8.81, 762.18) * mm});
            skLineSegment(sketch, "E256", {"start": v(-8.81, 754.18) * mm, "end": v(-8.81, 747.73) * mm});
            skLineSegment(sketch, "E257", {"start": v(-12.81, 764.15) * mm, "end": v(-12.81, 762.18) * mm});
            skLineSegment(sketch, "E258", {"start": v(-12.81, 754.18) * mm, "end": v(-12.81, 751.73) * mm});
            skLineSegment(sketch, "E259", {"start": v(-16.84, 764.15) * mm, "end": v(-16.84, 751.73) * mm});
            skLineSegment(sketch, "E260", {"start": v(28.61, 768.15) * mm, "end": v(28.61, 638.71) * mm});
            skLineSegment(sketch, "E261", {"start": v(7.9, 638.94) * mm, "end": v(7.9, 661.2) * mm});
            skLineSegment(sketch, "E262", {"start": v(7.9, 661.2) * mm, "end": v(11.9, 661.2) * mm});
            skLineSegment(sketch, "E263", {"start": v(11.9, 661.2) * mm, "end": v(11.9, 643.93) * mm});
            skSolve(sketch);
        }
        {
            var Q0;
            Q0 = qSketchRegion(id + "F11", true);
            extrude(context, id + "F12", {"entities" : qUnion([Q0]), "oppositeDirection" : true, "depth" : 1000 * mm, "offsetDistance" : 25 * mm});
        }
        {
            var Q0;
            Q0=makeQuery(id+"F4.opExtrude","CAP_FACE",FACE,{"disambiguationData":[OSD([sQuery(id+"F3.wireOp",EDGE,"E70"),sQuery(id+"F3.wireOp",EDGE,"E71"),sQuery(id+"F3.wireOp",EDGE,"E72"),sQuery(id+"F3.wireOp",EDGE,"E73"),sQuery(id+"F3.wireOp",EDGE,"E74"),sQuery(id+"F3.wireOp",EDGE,"E75"),sQuery(id+"F3.wireOp",EDGE,"E76"),sQuery(id+"F3.wireOp",EDGE,"E77"),sQuery(id+"F3.wireOp",EDGE,"E78"),sQuery(id+"F3.wireOp",EDGE,"E79"),sQuery(id+"F3.wireOp",EDGE,"E80"),sQuery(id+"F3.wireOp",EDGE,"E81"),sQuery(id+"F3.wireOp",EDGE,"E82"),sQuery(id+"F3.wireOp",EDGE,"E83"),sQuery(id+"F3.wireOp",EDGE,"E84"),sQuery(id+"F3.wireOp",EDGE,"E85"),sQuery(id+"F3.wireOp",EDGE,"E86"),sQuery(id+"F3.wireOp",EDGE,"E87"),sQuery(id+"F3.wireOp",EDGE,"E88"),sQuery(id+"F3.wireOp",EDGE,"E89"),sQuery(id+"F3.wireOp",EDGE,"E90"),sQuery(id+"F3.wireOp",EDGE,"E91"),sQuery(id+"F3.wireOp",EDGE,"E92"),sQuery(id+"F3.wireOp",EDGE,"E93"),sQuery(id+"F3.wireOp",EDGE,"E94"),sQuery(id+"F3.wireOp",EDGE,"E95"),sQuery(id+"F3.wireOp",EDGE,"E96"),sQuery(id+"F3.wireOp",EDGE,"E97"),sQuery(id+"F3.wireOp",EDGE,"E98"),sQuery(id+"F3.wireOp",EDGE,"E99"),sQuery(id+"F3.wireOp",EDGE,"E100"),sQuery(id+"F3.wireOp",EDGE,"E101"),sQuery(id+"F3.wireOp",EDGE,"E102"),sQuery(id+"F3.wireOp",EDGE,"E103"),sQuery(id+"F3.wireOp",EDGE,"E104"),sQuery(id+"F3.wireOp",EDGE,"E105"),sQuery(id+"F3.wireOp",EDGE,"E106"),sQuery(id+"F3.wireOp",EDGE,"E107"),sQuery(id+"F3.wireOp",EDGE,"E108"),sQuery(id+"F3.wireOp",EDGE,"E109"),sQuery(id+"F3.wireOp",EDGE,"E111"),sQuery(id+"F3.wireOp",EDGE,"E112"),sQuery(id+"F3.wireOp",EDGE,"E113"),sQuery(id+"F3.wireOp",EDGE,"E114"),sQuery(id+"F3.wireOp",EDGE,"E115"),sQuery(id+"F3.wireOp",EDGE,"E116"),sQuery(id+"F3.wireOp",EDGE,"E117"),sQuery(id+"F3.wireOp",EDGE,"E118"),sQuery(id+"F3.wireOp",EDGE,"E119"),sQuery(id+"F3.wireOp",EDGE,"E120"),sQuery(id+"F3.wireOp",EDGE,"E121"),sQuery(id+"F3.wireOp",EDGE,"E122"),sQuery(id+"F3.wireOp",EDGE,"E123"),sQuery(id+"F3.wireOp",EDGE,"E124"),sQuery(id+"F3.wireOp",EDGE,"E125"),sQuery(id+"F3.wireOp",EDGE,"E126"),sQuery(id+"F3.wireOp",EDGE,"E127"),sQuery(id+"F3.wireOp",EDGE,"E128"),sQuery(id+"F3.wireOp",EDGE,"E129"),sQuery(id+"F3.wireOp",EDGE,"E130"),sQuery(id+"F3.wireOp",EDGE,"E131"),sQuery(id+"F3.wireOp",EDGE,"E132"),sQuery(id+"F3.wireOp",EDGE,"E133"),sQuery(id+"F3.wireOp",EDGE,"E134"),sQuery(id+"F3.wireOp",EDGE,"E135"),sQuery(id+"F3.wireOp",EDGE,"E136"),sQuery(id+"F3.wireOp",EDGE,"E137.trimOffspring"),sQuery(id+"F3.wireOp",EDGE,"E138"),sQuery(id+"F3.wireOp",EDGE,"E139"),sQuery(id+"F3.wireOp",EDGE,"E140"),sQuery(id+"F3.wireOp",EDGE,"E141"),sQuery(id+"F3.wireOp",EDGE,"E142"),sQuery(id+"F3.wireOp",EDGE,"E143"),sQuery(id+"F3.wireOp",EDGE,"E144"),sQuery(id+"F3.wireOp",EDGE,"E145"),sQuery(id+"F3.wireOp",EDGE,"E146")])],"isStart":true});
            var sketch = newSketch(context, id + "F13", { "sketchPlane" : qUnion([Q0])});
            skLineSegment(sketch, "E264", {"start": v(-11.46, 78.29) * mm, "end": v(-11.46, 70.29) * mm});
            skLineSegment(sketch, "E265", {"start": v(-11.46, 70.29) * mm, "end": v(-23.46, 70.29) * mm});
            skLineSegment(sketch, "E266", {"start": v(-23.46, 70.29) * mm, "end": v(-23.46, 163.36) * mm});
            skLineSegment(sketch, "E267", {"start": v(-7, 150.71) * mm, "end": v(-3, 150.77) * mm});
            skLineSegment(sketch, "E268", {"start": v(-7, 150.71) * mm, "end": v(-7, 159.36) * mm});
            skLineSegment(sketch, "E269", {"start": v(-7, 159.36) * mm, "end": v(-19.46, 159.36) * mm});
            skLineSegment(sketch, "E270", {"start": v(-19.46, 159.36) * mm, "end": v(-19.46, 140.65) * mm});
            skLineSegment(sketch, "E271", {"start": v(-19.46, 140.65) * mm, "end": v(24.85, 140.65) * mm});
            skLineSegment(sketch, "E272", {"start": v(24.85, 140.65) * mm, "end": v(24.85, 159.36) * mm});
            skLineSegment(sketch, "E273", {"start": v(24.85, 159.36) * mm, "end": v(11, 159.36) * mm});
            skLineSegment(sketch, "E274", {"start": v(7, 163.36) * mm, "end": v(28.85, 163.36) * mm});
            skLineSegment(sketch, "E275", {"start": v(28.85, 163.36) * mm, "end": v(28.85, 70.29) * mm});
            skLineSegment(sketch, "E276", {"start": v(28.85, 70.29) * mm, "end": v(16.85, 70.29) * mm});
            skLineSegment(sketch, "E277", {"start": v(16.85, 70.29) * mm, "end": v(16.85, 78.29) * mm});
            skLineSegment(sketch, "E278", {"start": v(16.85, 78.29) * mm, "end": v(20.85, 78.29) * mm});
            skLineSegment(sketch, "E279.bottom", {"start": v(-19.46, 136.65) * mm, "end": v(24.85, 136.65) * mm});
            skLineSegment(sketch, "E279.top", {"start": v(-19.46, 106.9) * mm, "end": v(24.85, 106.9) * mm});
            skLineSegment(sketch, "E279.left", {"start": v(-19.46, 136.65) * mm, "end": v(-19.46, 106.9) * mm});
            skLineSegment(sketch, "E279.right", {"start": v(24.85, 136.65) * mm, "end": v(24.85, 106.9) * mm});
            skLineSegment(sketch, "E280", {"start": v(-11.46, 78.29) * mm, "end": v(-15.46, 78.29) * mm});
            skLineSegment(sketch, "E281", {"start": v(-15.46, 78.29) * mm, "end": v(-15.46, 74.29) * mm});
            skLineSegment(sketch, "E282", {"start": v(-15.46, 74.29) * mm, "end": v(-19.46, 74.29) * mm});
            skLineSegment(sketch, "E283", {"start": v(-19.46, 74.29) * mm, "end": v(-19.46, 102.9) * mm});
            skLineSegment(sketch, "E284", {"start": v(-19.46, 102.9) * mm, "end": v(24.85, 102.9) * mm});
            skLineSegment(sketch, "E285", {"start": v(24.85, 102.9) * mm, "end": v(24.85, 74.29) * mm});
            skLineSegment(sketch, "E286", {"start": v(24.85, 74.29) * mm, "end": v(20.84, 74.29) * mm});
            skLineSegment(sketch, "E287", {"start": v(-23.46, 163.36) * mm, "end": v(-3, 163.36) * mm});
            skLineSegment(sketch, "E288", {"start": v(-3, 163.36) * mm, "end": v(-3, 150.77) * mm});
            skLineSegment(sketch, "E289", {"start": v(7, 163.36) * mm, "end": v(7, 150.77) * mm});
            skLineSegment(sketch, "E290", {"start": v(7, 150.77) * mm, "end": v(11, 150.77) * mm});
            skLineSegment(sketch, "E291", {"start": v(11, 150.77) * mm, "end": v(11, 159.36) * mm});
            skLineSegment(sketch, "E292", {"start": v(20.85, 78.29) * mm, "end": v(20.84, 74.29) * mm});
            skLineSegment(sketch, "E293", {"start": v(2, 121.18) * mm, "end": v(2, 57.48) * mm, "construction": true});
            skPoint(sketch, "E293.startSnap0", {"position": v(2, 106.9) * mm});
            skLineSegment(sketch, "E294.bottom", {"start": v(-3, 163.36) * mm, "end": v(8, 163.36) * mm});
            skLineSegment(sketch, "E294.top", {"start": v(-3, 639.05) * mm, "end": v(8, 639.05) * mm});
            skLineSegment(sketch, "E294.left", {"start": v(-3, 163.36) * mm, "end": v(-3, 639.05) * mm});
            skLineSegment(sketch, "E294.right", {"start": v(8, 163.36) * mm, "end": v(8, 639.05) * mm});
            skSolve(sketch);
        }
        {
            var Q0;
            Q0=makeQuery(id+"F13.imprint","IMPRINT",FACE,{"disambiguationData":[TD([[makeQuery(id+"F13.imprint","IMPRINT",EDGE,{"derivedFrom":sQuery(id+"F13.wireOp",EDGE,"E264")}),-1.0]])]});
            extrude(context, id + "F14", {"entities" : qUnion([Q0]), "oppositeDirection" : true, "depth" : 1000 * mm, "offsetDistance" : 25 * mm});
        }
        {
            var Q0;
            Q0 = qSketchRegion(id + "F13", true);
            extrude(context, id + "F15", {"entities" : qUnion([Q0]), "oppositeDirection" : true, "depth" : 1000 * mm, "offsetDistance" : 25 * mm});
        }
        {
            var Q0;
            Q0=makeQuery(id+"F6.opExtrude","SWEPT_FACE",FACE,{"disambiguationData":[OSD([sQuery(id+"F5.wireOp",EDGE,"E189")])]});
            var sketch = newSketch(context, id + "F16", { "sketchPlane" : qUnion([Q0])});
            skLineSegment(sketch, "E295.bottom", {"start": v(308.57, 261.27) * mm, "end": v(1308.57, 261.27) * mm});
            skLineSegment(sketch, "E295.top", {"start": v(308.57, 257.27) * mm, "end": v(1308.57, 257.27) * mm});
            skLineSegment(sketch, "E295.left", {"start": v(308.57, 261.27) * mm, "end": v(308.57, 257.27) * mm});
            skLineSegment(sketch, "E295.right", {"start": v(1308.57, 261.27) * mm, "end": v(1308.57, 257.27) * mm});
            skSolve(sketch);
        }
        {
            var Q0;
            Q0=makeQuery(id+"F16.imprint","IMPRINT",FACE,{"disambiguationData":[TD([[makeQuery(id+"F16.imprint","IMPRINT",EDGE,{"derivedFrom":sQuery(id+"F16.wireOp",EDGE,"E295.bottom")}),-1.0]])]});
            extrude(context, id + "F17", {"entities" : qUnion([Q0]), "depth" : 1700 * mm, "offsetDistance" : 25 * mm});
        }
    });
